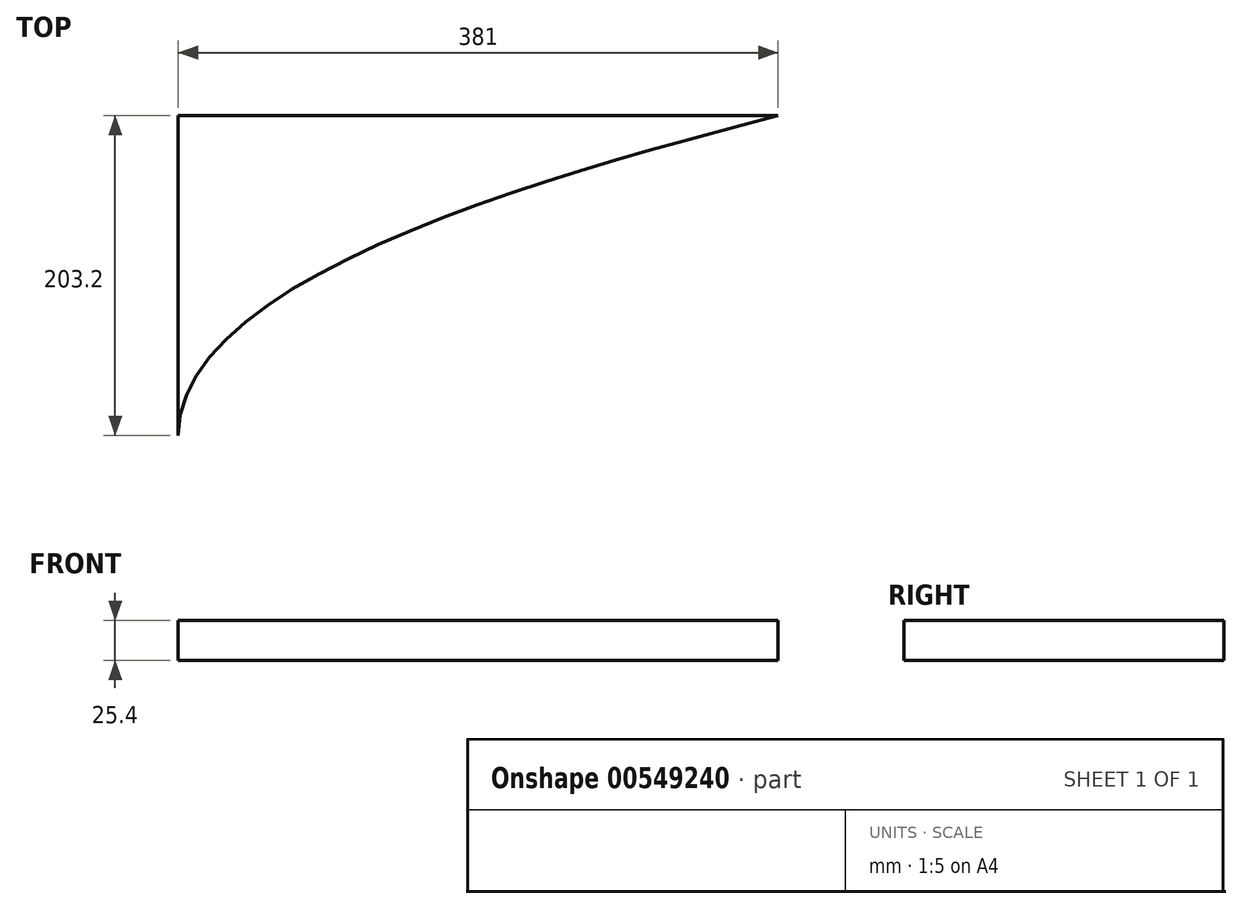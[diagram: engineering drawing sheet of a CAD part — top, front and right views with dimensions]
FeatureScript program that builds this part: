
annotation { "Feature Type Name" : "Feature", "Feature Type Description" : "" }
export const myFeature = defineFeature(function(context is Context, id is Id, definition is map)
    precondition{}
    {
        {
            var Q0;
            Q0=qCreatedBy(makeId("Top.planeOp"),FACE);
            var sketch = newSketch(context, id + "F0", { "sketchPlane" : qUnion([Q0])});
            skLineSegment(sketch, "E0", {"start": v(-179.72, 100.18) * mm, "end": v(201.28, 100.18) * mm});
            skLineSegment(sketch, "E1", {"start": v(-179.72, 100.18) * mm, "end": v(-179.72, -103.02) * mm});
            skFitSpline(sketch, "E2", {"points": [v(-179.72, -103.02) * mm, v(201.28, 100.18) * mm], "startDerivative": vector(0, 304.8) * mm, "endDerivative": vector(427.88, 112.9) * mm});
            skSolve(sketch);
        }
        {
            var Q0;
            Q0 = qSketchRegion(id + "F0", true);
            extrude(context, id + "F1", {"entities" : qUnion([Q0]), "depth" : 25.4 * mm, "offsetDistance" : 25.4 * mm});
        }
    });
